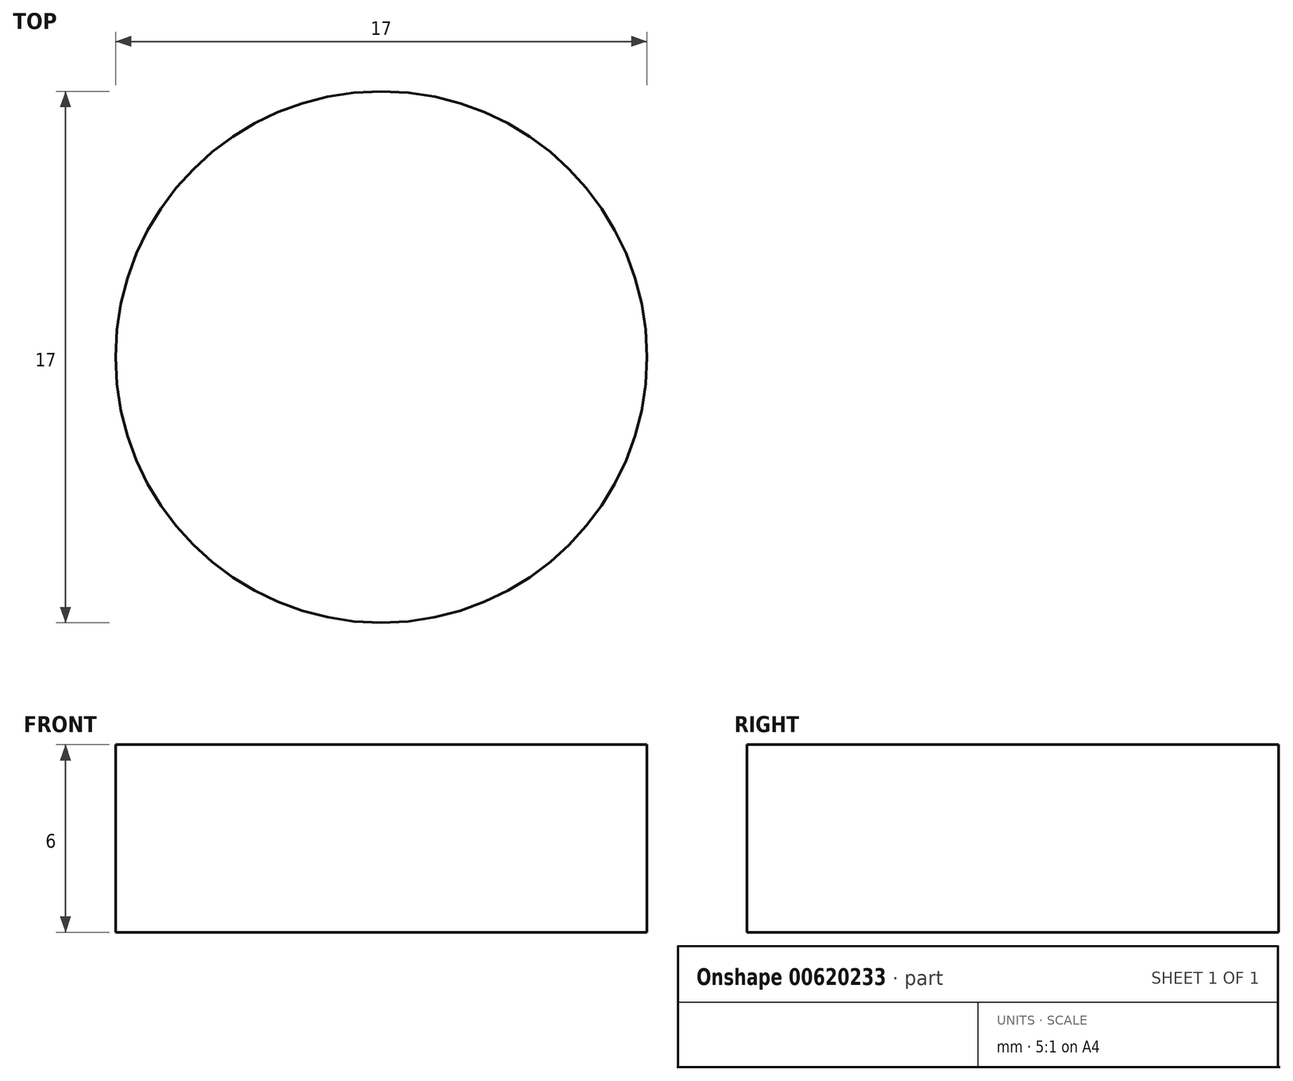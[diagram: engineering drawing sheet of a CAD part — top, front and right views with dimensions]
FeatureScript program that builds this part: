
annotation { "Feature Type Name" : "Feature", "Feature Type Description" : "" }
export const myFeature = defineFeature(function(context is Context, id is Id, definition is map)
    precondition{}
    {
        {
            var Q0;
            Q0=qCreatedBy(makeId("Top.planeOp"),FACE);
            var sketch = newSketch(context, id + "F0", { "sketchPlane" : qUnion([Q0])});
            skCircle(sketch, "E0", {"center": v(0, 0) * mm, "radius": 8.5 * mm});
            skSolve(sketch);
        }
        {
            var Q0;
            Q0=makeQuery(id+"F0.imprint","IMPRINT",FACE,{"disambiguationData":[TD([[makeQuery(id+"F0.imprint","IMPRINT",EDGE,{"derivedFrom":sQuery(id+"F0.wireOp",EDGE,"E0")}),1.0]])]});
            extrude(context, id + "F1", {"entities" : qUnion([Q0]), "depth" : 6 * mm, "offsetDistance" : 25 * mm});
        }
    });
